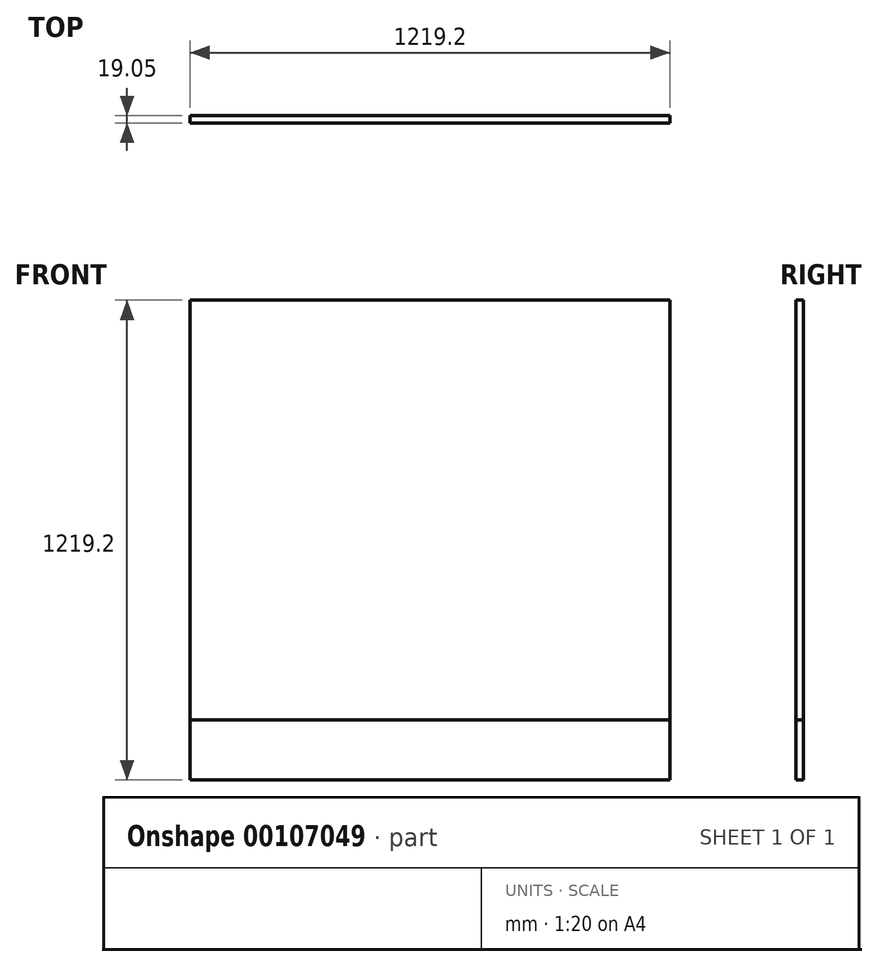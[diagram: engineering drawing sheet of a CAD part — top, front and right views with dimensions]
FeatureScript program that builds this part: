
annotation { "Feature Type Name" : "Feature", "Feature Type Description" : "" }
export const myFeature = defineFeature(function(context is Context, id is Id, definition is map)
    precondition{}
    {
        {
            var Q0;
            Q0=qCreatedBy(makeId("Front.planeOp"),FACE);
            var sketch = newSketch(context, id + "F0", { "sketchPlane" : qUnion([Q0])});
            skLineSegment(sketch, "E0.bottom", {"start": v(-1182.41, 856.74) * mm, "end": v(36.79, 856.74) * mm});
            skLineSegment(sketch, "E0.top", {"start": v(-1182.41, -210.06) * mm, "end": v(36.79, -210.06) * mm});
            skLineSegment(sketch, "E0.left", {"start": v(-1182.41, 856.74) * mm, "end": v(-1182.41, -210.06) * mm});
            skLineSegment(sketch, "E0.right", {"start": v(36.79, 856.74) * mm, "end": v(36.79, -210.06) * mm});
            skLineSegment(sketch, "E1.top", {"start": v(-1182.41, -362.46) * mm, "end": v(36.79, -362.46) * mm});
            skLineSegment(sketch, "E1.left", {"start": v(-1182.41, -210.06) * mm, "end": v(-1182.41, -362.46) * mm});
            skLineSegment(sketch, "E1.right", {"start": v(36.79, -210.06) * mm, "end": v(36.79, -362.46) * mm});
            skSolve(sketch);
        }
        {
            var Q0;
            Q0=makeQuery(id+"F0.imprint","IMPRINT",FACE,{"disambiguationData":[TD([[makeQuery(id+"F0.imprint","IMPRINT",EDGE,{"derivedFrom":sQuery(id+"F0.wireOp",EDGE,"E0.bottom")}),-1.0]])]});
            extrude(context, id + "F1", {"entities" : qUnion([Q0]), "depth" : 19.05 * mm});
        }
        {
            var Q0;
            Q0=makeQuery(id+"F0.imprint","IMPRINT",FACE,{"disambiguationData":[TD([[makeQuery(id+"F0.imprint","IMPRINT",EDGE,{"derivedFrom":sQuery(id+"F0.wireOp",EDGE,"E0.top")}),-1.0]])]});
            extrude(context, id + "F2", {"entities" : qUnion([Q0]), "depth" : 19.05 * mm});
        }
    });
